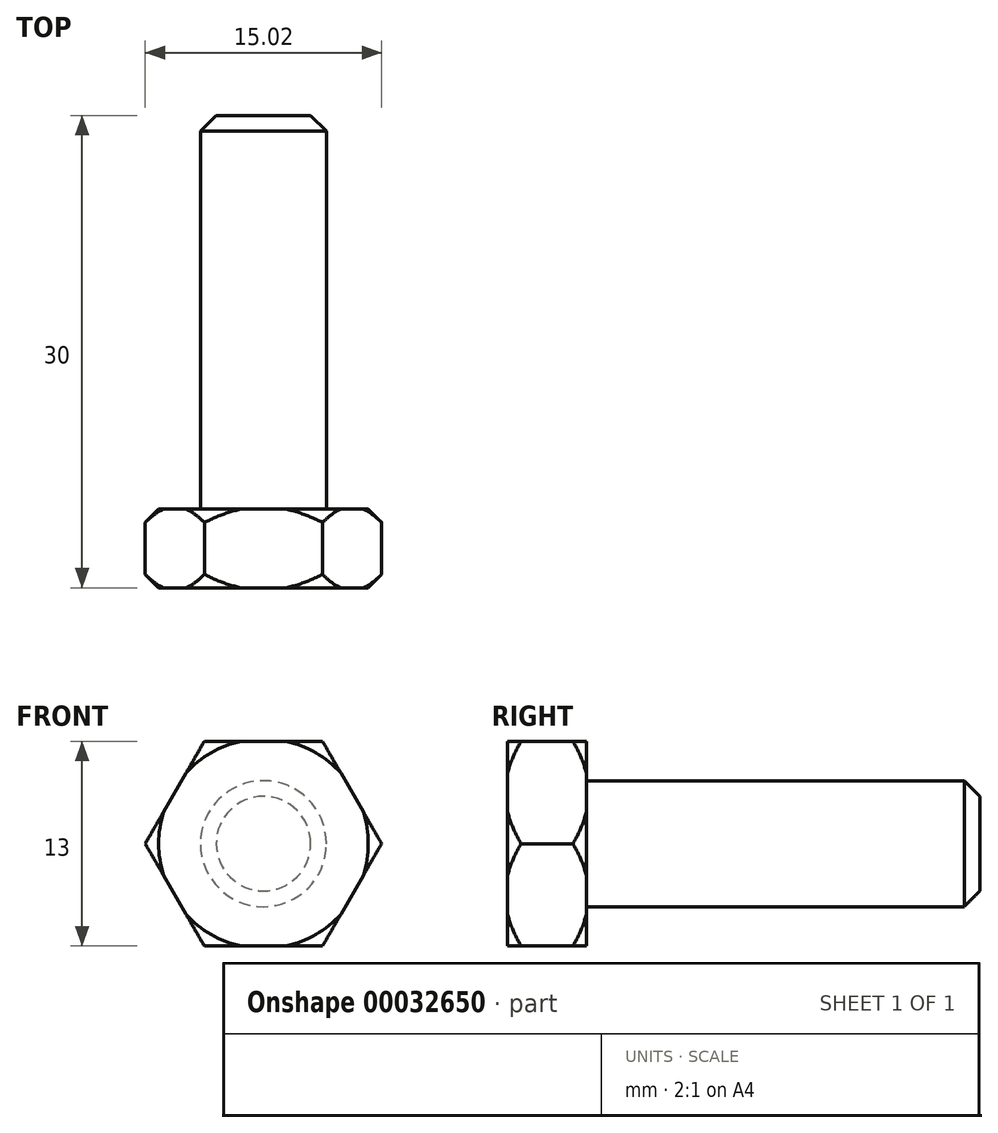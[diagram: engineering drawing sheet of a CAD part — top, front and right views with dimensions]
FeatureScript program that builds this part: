
annotation { "Feature Type Name" : "Feature", "Feature Type Description" : "" }
export const myFeature = defineFeature(function(context is Context, id is Id, definition is map)
    precondition{}
    {
        {
            var Q0;
            Q0=qCreatedBy(makeId("Front.planeOp"),FACE);
            var sketch = newSketch(context, id + "F0", { "sketchPlane" : qUnion([Q0])});
            skCircle(sketch, "E0", {"center": v(0, 0) * mm, "radius": 4 * mm});
            skCircle(sketch, "E1", {"center": v(0, 0) * mm, "radius": 6.5 * mm});
            skCircle(sketch, "E2.cCircle", {"center": v(0, 0) * mm, "radius": 6.5 * mm, "construction": true});
            skLineSegment(sketch, "E2.0", {"start": v(-3.75, 6.5) * mm, "end": v(3.75, 6.5) * mm});
            skLineSegment(sketch, "E2.1", {"start": v(3.75, 6.5) * mm, "end": v(7.5, 0) * mm});
            skLineSegment(sketch, "E2.2", {"start": v(7.5, 0) * mm, "end": v(3.75, -6.5) * mm});
            skLineSegment(sketch, "E2.3", {"start": v(3.75, -6.5) * mm, "end": v(-3.75, -6.5) * mm});
            skLineSegment(sketch, "E2.4", {"start": v(-3.75, -6.5) * mm, "end": v(-7.5, 0) * mm});
            skLineSegment(sketch, "E2.5", {"start": v(-7.5, 0) * mm, "end": v(-3.75, 6.5) * mm});
            skPoint(sketch, "E2.0.midPoint", {"position": v(0, 6.5) * mm});
            skSolve(sketch);
        }
        {
            var Q0;
            Q0=makeQuery(id+"F0.imprint","IMPRINT",FACE,{"disambiguationData":[TD([[makeQuery(id+"F0.imprint","IMPRINT",EDGE,{"derivedFrom":sQuery(id+"F0.wireOp",EDGE,"E0")}),-1.0]])]});
            var Q1;
            Q1=makeQuery(id+"F0.imprint","IMPRINT",FACE,{"disambiguationData":[TD([[makeQuery(id+"F0.imprint","IMPRINT",EDGE,{"derivedFrom":sQuery(id+"F0.wireOp",EDGE,"E0")}),1.0]])]});
            var Q2;
            {var subQ1=sQuery(id+"F0.wireOp",EDGE,"E1");var subQ3=sQuery(id+"F0.wireOp",EDGE,"E2.1");var subQ5=makeQuery(id+"F0.imprint","INTERSECT",VERTEX,{"derivedFrom":[subQ1,subQ3]});Q2=makeQuery(id+"F0.imprint","IMPRINT",FACE,{"disambiguationData":[TD([[makeQuery(id+"F0.imprint","IMPRINT",EDGE,{"disambiguationData":[TD([[subQ5,1.0]])],"derivedFrom":subQ1}),-1.0]])]});}
            var Q3;
            {var subQ0=sQuery(id+"F0.wireOp",EDGE,"E2.3");var subQ1=sQuery(id+"F0.wireOp",EDGE,"E1");var subQ2=makeQuery(id+"F0.imprint","INTERSECT",VERTEX,{"derivedFrom":[subQ1,subQ0]});Q3=makeQuery(id+"F0.imprint","IMPRINT",FACE,{"disambiguationData":[TD([[makeQuery(id+"F0.imprint","IMPRINT",EDGE,{"disambiguationData":[TD([[subQ2,-1.0]])],"derivedFrom":subQ1}),-1.0]])]});}
            var Q4;
            {var subQ1=sQuery(id+"F0.wireOp",EDGE,"E1");var subQ3=sQuery(id+"F0.wireOp",EDGE,"E2.0");var subQ5=makeQuery(id+"F0.imprint","INTERSECT",VERTEX,{"derivedFrom":[subQ1,subQ3]});Q4=makeQuery(id+"F0.imprint","IMPRINT",FACE,{"disambiguationData":[TD([[makeQuery(id+"F0.imprint","IMPRINT",EDGE,{"disambiguationData":[TD([[subQ5,1.0]])],"derivedFrom":subQ1}),-1.0]])]});}
            var Q5;
            {var subQ1=sQuery(id+"F0.wireOp",EDGE,"E1");var subQ3=sQuery(id+"F0.wireOp",EDGE,"E2.0");var subQ5=makeQuery(id+"F0.imprint","INTERSECT",VERTEX,{"derivedFrom":[subQ1,subQ3]});Q5=makeQuery(id+"F0.imprint","IMPRINT",FACE,{"disambiguationData":[TD([[makeQuery(id+"F0.imprint","IMPRINT",EDGE,{"disambiguationData":[TD([[subQ5,-1.0]])],"derivedFrom":subQ1}),-1.0]])]});}
            var Q6;
            {var subQ0=sQuery(id+"F0.wireOp",EDGE,"E2.5");var subQ1=sQuery(id+"F0.wireOp",EDGE,"E1");var subQ2=makeQuery(id+"F0.imprint","INTERSECT",VERTEX,{"derivedFrom":[subQ1,subQ0]});Q6=makeQuery(id+"F0.imprint","IMPRINT",FACE,{"disambiguationData":[TD([[makeQuery(id+"F0.imprint","IMPRINT",EDGE,{"disambiguationData":[TD([[subQ2,-1.0]])],"derivedFrom":subQ1}),-1.0]])]});}
            var Q7;
            {var subQ0=sQuery(id+"F0.wireOp",EDGE,"E2.4");var subQ1=sQuery(id+"F0.wireOp",EDGE,"E1");var subQ2=makeQuery(id+"F0.imprint","INTERSECT",VERTEX,{"derivedFrom":[subQ1,subQ0]});Q7=makeQuery(id+"F0.imprint","IMPRINT",FACE,{"disambiguationData":[TD([[makeQuery(id+"F0.imprint","IMPRINT",EDGE,{"disambiguationData":[TD([[subQ2,-1.0]])],"derivedFrom":subQ1}),-1.0]])]});}
            extrude(context, id + "F1", {"entities" : qUnion([Q0, Q1, Q2, Q3, Q4, Q5, Q6, Q7]), "depth" : 5 * mm});
        }
        {
            var Q0;
            Q0=makeQuery(id+"F0.imprint","IMPRINT",FACE,{"disambiguationData":[TD([[makeQuery(id+"F0.imprint","IMPRINT",EDGE,{"derivedFrom":sQuery(id+"F0.wireOp",EDGE,"E0")}),1.0]])]});
            extrude(context, id + "F2", {"entities" : qUnion([Q0]), "operationType" : NewBodyOperationType.ADD, "oppositeDirection" : true, "depth" : 25 * mm});
        }
        {
            var Q0;
            Q0=makeQuery(id+"F2.opExtrude","CAP_EDGE",EDGE,{"disambiguationData":[OSD([sQuery(id+"F0.wireOp",EDGE,"E0")])],"isStart":false});
            chamfer(context, id + "F3", {"entities" : qUnion([Q0]), "width" : 1 * mm, "tangentPropagation" : true});
        }
        {
            var Q0;
            Q0=qCreatedBy(makeId("Right.planeOp"),FACE);
            var sketch = newSketch(context, id + "F4", { "sketchPlane" : qUnion([Q0])});
            skLineSegment(sketch, "E3", {"start": v(-5, 0) * mm, "end": v(25, 0) * mm, "construction": true});
            skLineSegment(sketch, "E4", {"start": v(-7.54, 4.12) * mm, "end": v(-4, 7.66) * mm});
            skLineSegment(sketch, "E5", {"start": v(-4, 7.66) * mm, "end": v(-1, 7.66) * mm});
            skLineSegment(sketch, "E6", {"start": v(-1, 7.66) * mm, "end": v(2.54, 4.12) * mm});
            skLineSegment(sketch, "E7", {"start": v(-2.5, 7.66) * mm, "end": v(-2.5, 6.5) * mm});
            skLineSegment(sketch, "E8", {"start": v(-7.54, 4.12) * mm, "end": v(-7.54, 9.52) * mm});
            skLineSegment(sketch, "E9", {"start": v(-7.54, 9.52) * mm, "end": v(2.54, 9.52) * mm});
            skLineSegment(sketch, "E10", {"start": v(2.54, 9.52) * mm, "end": v(2.54, 4.12) * mm});
            skSolve(sketch);
        }
        {
            var Q0;
            Q0 = qSketchRegion(id + "F4", true);
            var Q1;
            Q1=sQuery(id+"F4.wireOp",EDGE,"E3");
            revolve(context, id + "F5", {"operationType" : NewBodyOperationType.REMOVE, "entities" : qUnion([Q0]), "axis" : qUnion([Q1]), "revolveType" : RevolveType.FULL, "oppositeDirection" : true});
        }
    });
